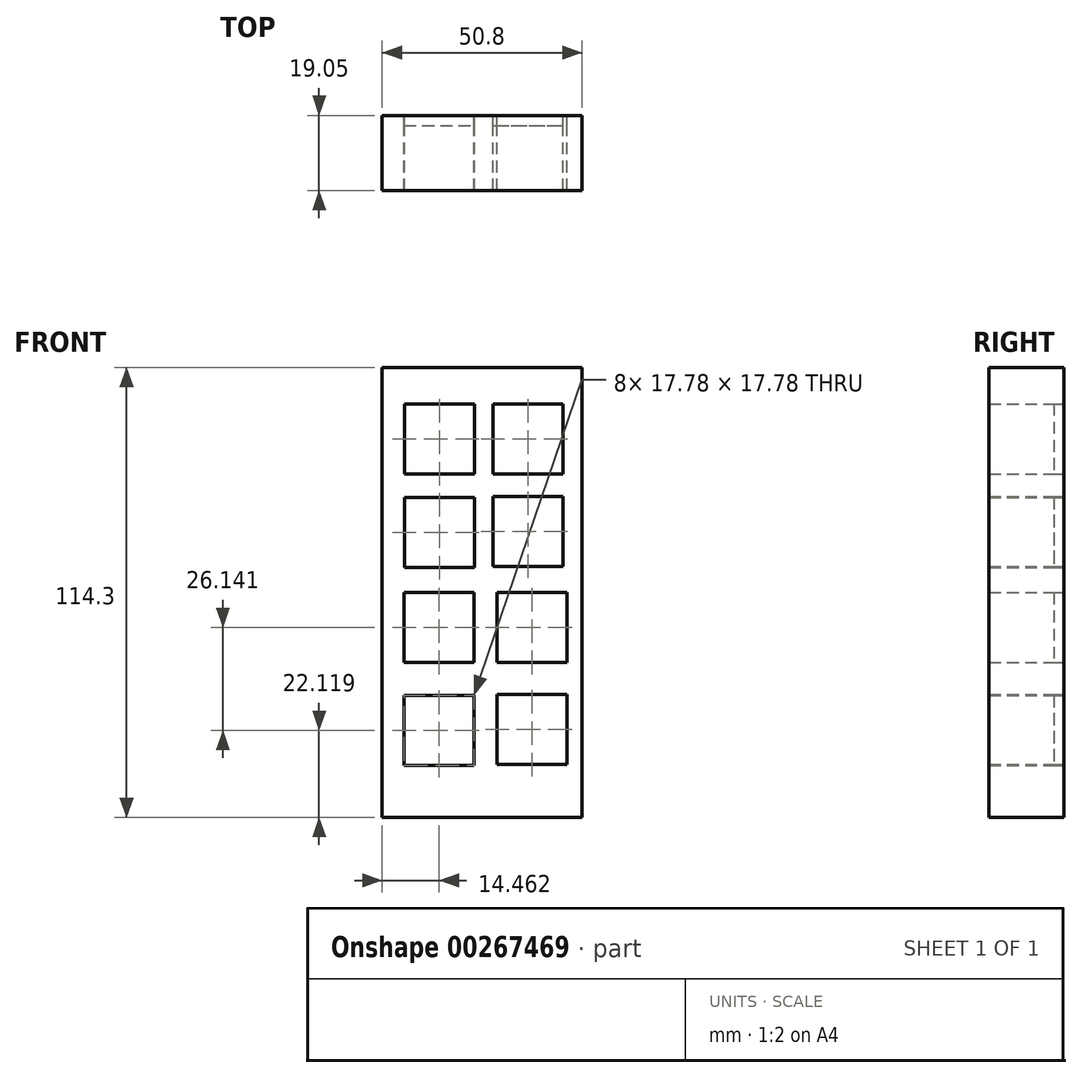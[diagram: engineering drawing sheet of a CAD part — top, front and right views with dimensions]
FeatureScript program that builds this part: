
annotation { "Feature Type Name" : "Feature", "Feature Type Description" : "" }
export const myFeature = defineFeature(function(context is Context, id is Id, definition is map)
    precondition{}
    {
        {
            var Q0;
            Q0=qCreatedBy(makeId("Front.planeOp"),FACE);
            var sketch = newSketch(context, id + "F0", { "sketchPlane" : qUnion([Q0])});
            skLineSegment(sketch, "E0.bottom", {"start": v(-25.4, 57.15) * mm, "end": v(25.4, 57.15) * mm});
            skLineSegment(sketch, "E0.top", {"start": v(-25.4, -57.15) * mm, "end": v(25.4, -57.15) * mm});
            skLineSegment(sketch, "E0.left", {"start": v(-25.4, 57.15) * mm, "end": v(-25.4, -57.15) * mm});
            skLineSegment(sketch, "E0.right", {"start": v(25.4, 57.15) * mm, "end": v(25.4, -57.15) * mm});
            skPoint(sketch, "E0.middle", {"position": v(0, 0) * mm});
            skLineSegment(sketch, "E1.bottom", {"start": v(-19.75, 47.93) * mm, "end": v(-1.97, 47.93) * mm});
            skLineSegment(sketch, "E1.top", {"start": v(-19.75, 30.15) * mm, "end": v(-1.97, 30.15) * mm});
            skLineSegment(sketch, "E1.left", {"start": v(-19.75, 47.93) * mm, "end": v(-19.75, 30.15) * mm});
            skLineSegment(sketch, "E1.right", {"start": v(-1.97, 47.93) * mm, "end": v(-1.97, 30.15) * mm});
            skLineSegment(sketch, "E2.bottom", {"start": v(2.72, 47.93) * mm, "end": v(20.5, 47.93) * mm});
            skLineSegment(sketch, "E2.top", {"start": v(2.72, 30.15) * mm, "end": v(20.5, 30.15) * mm});
            skLineSegment(sketch, "E2.left", {"start": v(2.72, 47.93) * mm, "end": v(2.72, 30.15) * mm});
            skLineSegment(sketch, "E2.right", {"start": v(20.5, 47.93) * mm, "end": v(20.5, 30.15) * mm});
            skLineSegment(sketch, "E3.bottom", {"start": v(-19.75, 24.09) * mm, "end": v(-1.97, 24.09) * mm});
            skLineSegment(sketch, "E3.top", {"start": v(-19.75, 6.3) * mm, "end": v(-1.97, 6.3) * mm});
            skLineSegment(sketch, "E3.left", {"start": v(-19.75, 24.09) * mm, "end": v(-19.75, 6.3) * mm});
            skLineSegment(sketch, "E3.right", {"start": v(-1.97, 24.09) * mm, "end": v(-1.97, 6.3) * mm});
            skLineSegment(sketch, "E4.bottom", {"start": v(2.72, 24.45) * mm, "end": v(20.5, 24.45) * mm});
            skLineSegment(sketch, "E4.top", {"start": v(2.72, 6.67) * mm, "end": v(20.5, 6.67) * mm});
            skLineSegment(sketch, "E4.left", {"start": v(2.72, 24.45) * mm, "end": v(2.72, 6.67) * mm});
            skLineSegment(sketch, "E4.right", {"start": v(20.5, 24.45) * mm, "end": v(20.5, 6.67) * mm});
            skLineSegment(sketch, "E5.bottom", {"start": v(-19.83, 0) * mm, "end": v(-2.05, 0) * mm});
            skLineSegment(sketch, "E5.top", {"start": v(-19.83, -17.78) * mm, "end": v(-2.05, -17.78) * mm});
            skLineSegment(sketch, "E5.left", {"start": v(-19.83, 0) * mm, "end": v(-19.83, -17.78) * mm});
            skLineSegment(sketch, "E5.right", {"start": v(-2.05, 0) * mm, "end": v(-2.05, -17.78) * mm});
            skLineSegment(sketch, "E6.bottom", {"start": v(3.8, 0) * mm, "end": v(21.58, 0) * mm});
            skLineSegment(sketch, "E6.top", {"start": v(3.8, -17.78) * mm, "end": v(21.58, -17.78) * mm});
            skLineSegment(sketch, "E6.left", {"start": v(3.8, 0) * mm, "end": v(3.8, -17.78) * mm});
            skLineSegment(sketch, "E6.right", {"start": v(21.58, 0) * mm, "end": v(21.58, -17.78) * mm});
            skLineSegment(sketch, "E7.bottom", {"start": v(-19.83, -26.14) * mm, "end": v(-2.05, -26.14) * mm});
            skLineSegment(sketch, "E7.top", {"start": v(-19.83, -43.92) * mm, "end": v(-2.05, -43.92) * mm});
            skLineSegment(sketch, "E7.left", {"start": v(-19.83, -26.14) * mm, "end": v(-19.83, -43.92) * mm});
            skLineSegment(sketch, "E7.right", {"start": v(-2.05, -26.14) * mm, "end": v(-2.05, -43.92) * mm});
            skLineSegment(sketch, "E8.bottom", {"start": v(3.8, -25.96) * mm, "end": v(21.58, -25.96) * mm});
            skLineSegment(sketch, "E8.top", {"start": v(3.8, -43.74) * mm, "end": v(21.58, -43.74) * mm});
            skLineSegment(sketch, "E8.left", {"start": v(3.8, -25.96) * mm, "end": v(3.8, -43.74) * mm});
            skLineSegment(sketch, "E8.right", {"start": v(21.58, -25.96) * mm, "end": v(21.58, -43.74) * mm});
            skSolve(sketch);
        }
        {
            var Q0;
            Q0 = qSketchRegion(id + "F0", true);
            extrude(context, id + "F1", {"entities" : qUnion([Q0]), "depth" : 19.05 * mm});
        }
        {
            var Q0;
            Q0=makeQuery(id+"F0.imprint","IMPRINT",FACE,{"disambiguationData":[TD([[makeQuery(id+"F0.imprint","IMPRINT",EDGE,{"derivedFrom":sQuery(id+"F0.wireOp",EDGE,"E6.bottom")}),-1.0]])]});
            var Q1;
            Q1=makeQuery(id+"F0.imprint","IMPRINT",FACE,{"disambiguationData":[TD([[makeQuery(id+"F0.imprint","IMPRINT",EDGE,{"derivedFrom":sQuery(id+"F0.wireOp",EDGE,"E4.bottom")}),-1.0]])]});
            var Q2;
            Q2=makeQuery(id+"F0.imprint","IMPRINT",FACE,{"disambiguationData":[TD([[makeQuery(id+"F0.imprint","IMPRINT",EDGE,{"derivedFrom":sQuery(id+"F0.wireOp",EDGE,"E2.bottom")}),-1.0]])]});
            var Q3;
            Q3=makeQuery(id+"F0.imprint","IMPRINT",FACE,{"disambiguationData":[TD([[makeQuery(id+"F0.imprint","IMPRINT",EDGE,{"derivedFrom":sQuery(id+"F0.wireOp",EDGE,"E1.bottom")}),-1.0]])]});
            var Q4;
            Q4=makeQuery(id+"F0.imprint","IMPRINT",FACE,{"disambiguationData":[TD([[makeQuery(id+"F0.imprint","IMPRINT",EDGE,{"derivedFrom":sQuery(id+"F0.wireOp",EDGE,"E3.bottom")}),-1.0]])]});
            var Q5;
            Q5=makeQuery(id+"F0.imprint","IMPRINT",FACE,{"disambiguationData":[TD([[makeQuery(id+"F0.imprint","IMPRINT",EDGE,{"derivedFrom":sQuery(id+"F0.wireOp",EDGE,"E5.bottom")}),-1.0]])]});
            var Q6;
            Q6=makeQuery(id+"F0.imprint","IMPRINT",FACE,{"disambiguationData":[TD([[makeQuery(id+"F0.imprint","IMPRINT",EDGE,{"derivedFrom":sQuery(id+"F0.wireOp",EDGE,"E7.bottom")}),-1.0]])]});
            var Q7;
            Q7=makeQuery(id+"F0.imprint","IMPRINT",FACE,{"disambiguationData":[TD([[makeQuery(id+"F0.imprint","IMPRINT",EDGE,{"derivedFrom":sQuery(id+"F0.wireOp",EDGE,"E8.bottom")}),-1.0]])]});
            extrude(context, id + "F2", {"entities" : qUnion([Q0, Q1, Q2, Q3, Q4, Q5, Q6, Q7]), "depth" : 2.54 * mm});
        }
    });
